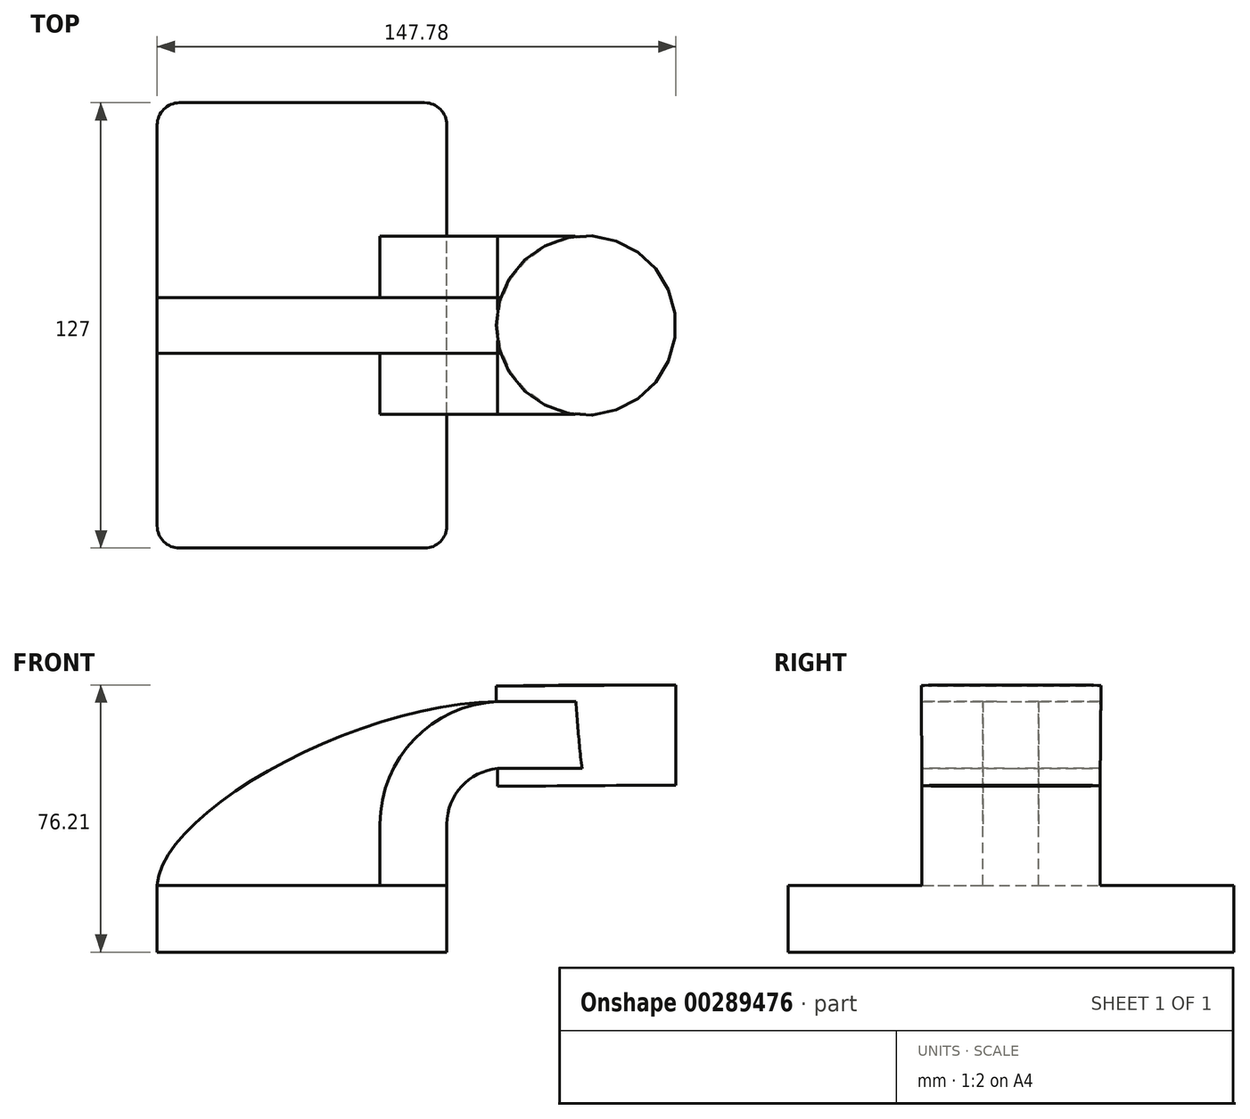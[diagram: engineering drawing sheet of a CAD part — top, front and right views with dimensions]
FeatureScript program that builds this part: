
annotation { "Feature Type Name" : "Feature", "Feature Type Description" : "" }
export const myFeature = defineFeature(function(context is Context, id is Id, definition is map)
    precondition{}
    {
        {
            var Q0;
            Q0=qCreatedBy(makeId("Front.planeOp"),FACE);
            var sketch = newSketch(context, id + "F0", { "sketchPlane" : qUnion([Q0])});
            skLineSegment(sketch, "E0.bottom", {"start": v(-41.28, 9.52) * mm, "end": v(41.27, 9.53) * mm});
            skLineSegment(sketch, "E0.top", {"start": v(-41.27, -9.53) * mm, "end": v(41.28, -9.53) * mm});
            skLineSegment(sketch, "E0.left", {"start": v(-41.28, 9.52) * mm, "end": v(-41.28, -9.53) * mm});
            skLineSegment(sketch, "E0.right", {"start": v(41.28, 9.53) * mm, "end": v(41.28, -9.52) * mm});
            skPoint(sketch, "E0.middle", {"position": v(0, 0) * mm});
            skLineSegment(sketch, "E1.bottom", {"start": v(55.7, 66.68) * mm, "end": v(106.5, 66.68) * mm});
            skLineSegment(sketch, "E1.top", {"start": v(55.7, 38.1) * mm, "end": v(106.5, 38.1) * mm});
            skLineSegment(sketch, "E1.left", {"start": v(55.7, 66.68) * mm, "end": v(55.7, 38.1) * mm});
            skLineSegment(sketch, "E1.right", {"start": v(106.5, 66.68) * mm, "end": v(106.5, 38.1) * mm});
            skPoint(sketch, "E1.middle", {"position": v(81.1, 52.39) * mm});
            skLineSegment(sketch, "E2", {"start": v(41.28, 9.53) * mm, "end": v(41.28, 27) * mm});
            skArc(sketch, "E3", {"start": v(41.28, 27) * mm, "mid": v(45.92, 38.23) * mm, "end": v(57.15, 42.88) * mm});
            skLineSegment(sketch, "E4", {"start": v(57.15, 42.88) * mm, "end": v(80.9, 42.88) * mm});
            skLineSegment(sketch, "E5.0", {"start": v(57.15, 61.93) * mm, "end": v(80.9, 61.93) * mm});
            skArc(sketch, "E5.1", {"start": v(22.23, 27) * mm, "mid": v(32.45, 51.7) * mm, "end": v(57.15, 61.93) * mm});
            skLineSegment(sketch, "E5.2", {"start": v(22.23, 9.53) * mm, "end": v(22.23, 27) * mm});
            skLineSegment(sketch, "E6", {"start": v(81.1, 38.1) * mm, "end": v(80.9, 66.68) * mm});
            skFitSpline(sketch, "E7", {"points": [v(-41.28, 9.52) * mm, v(57.15, 61.93) * mm], "startDerivative": vector(3.47, 63.91) * mm, "endDerivative": vector(119.87, -0.98) * mm});
            skSolve(sketch);
        }
        {
            var Q0;
            Q0=makeQuery(id+"F0.imprint","IMPRINT",FACE,{"disambiguationData":[TD([[makeQuery(id+"F0.imprint","IMPRINT",EDGE,{"derivedFrom":sQuery(id+"F0.wireOp",EDGE,"E0.top")}),1.0]])]});
            extrude(context, id + "F1", {"entities" : qUnion([Q0]), "endBound" : BoundingType.SYMMETRIC, "depth" : 127 * mm});
        }
        {
            var Q0;
            {var subQ1=sQuery(id+"F0.wireOp",EDGE,"E2");Q0=makeQuery(id+"F0.imprint","IMPRINT",FACE,{"disambiguationData":[TD([[makeQuery(id+"F0.imprint","IMPRINT",EDGE,{"derivedFrom":subQ1}),1.0]])]});}
            extrude(context, id + "F2", {"entities" : qUnion([Q0]), "operationType" : NewBodyOperationType.ADD, "endBound" : BoundingType.SYMMETRIC, "depth" : 50.8 * mm});
        }
        {
            var Q0;
            {var subQ0=sQuery(id+"F0.wireOp",EDGE,"E5.2");Q0=makeQuery(id+"F0.imprint","IMPRINT",FACE,{"disambiguationData":[TD([[makeQuery(id+"F0.imprint","IMPRINT",EDGE,{"derivedFrom":subQ0}),1.0]])]});}
            extrude(context, id + "F3", {"entities" : qUnion([Q0]), "operationType" : NewBodyOperationType.ADD, "endBound" : BoundingType.SYMMETRIC, "depth" : 15.88 * mm});
        }
        {
            var Q0;
            {var subQ0=sQuery(id+"F0.wireOp",EDGE,"E1.left");Q0=makeQuery(id+"F3.boolean.opBoolean","MERGE",FACE,{"derivedFrom":[makeQuery(id+"F2.opExtrude","SWEPT_FACE",FACE,{"disambiguationData":[OSD([subQ0])]}),makeQuery(id+"F3.opExtrude","SWEPT_FACE",FACE,{"disambiguationData":[OSD([subQ0])]})]});}
            extrude(context, id + "F4", {"entities" : qUnion([Q0]), "operationType" : NewBodyOperationType.ADD, "depth" : 25.4 * mm});
        }
        {
            var Q0;
            {var subQ0=sQuery(id+"F0.wireOp",EDGE,"E1.right");Q0=makeQuery(id+"F0.imprint","IMPRINT",FACE,{"disambiguationData":[TD([[makeQuery(id+"F0.imprint","IMPRINT",EDGE,{"derivedFrom":subQ0}),-1.0]])]});}
            var Q1;
            Q1=sQuery(id+"F0.wireOp",EDGE,"E6");
            revolve(context, id + "F5", {"operationType" : NewBodyOperationType.ADD, "entities" : qUnion([Q0]), "axis" : qUnion([Q1]), "revolveType" : RevolveType.FULL});
        }
        {
            var Q0;
            Q0=makeQuery(id+"F1.opExtrude","CAP_EDGE",EDGE,{"disambiguationData":[OSD([sQuery(id+"F0.wireOp",EDGE,"E0.left")])],"isStart":true});
            var Q1;
            Q1=makeQuery(id+"F1.opExtrude","CAP_EDGE",EDGE,{"disambiguationData":[OSD([sQuery(id+"F0.wireOp",EDGE,"E0.left")])],"isStart":false});
            var Q2;
            Q2=makeQuery(id+"F1.opExtrude","CAP_EDGE",EDGE,{"disambiguationData":[OSD([sQuery(id+"F0.wireOp",EDGE,"E0.right")])],"isStart":false});
            var Q3;
            Q3=makeQuery(id+"F1.opExtrude","CAP_EDGE",EDGE,{"disambiguationData":[OSD([sQuery(id+"F0.wireOp",EDGE,"E0.right")])],"isStart":true});
            fillet(context, id + "F6", {"entities" : qUnion([Q0, Q1, Q2, Q3]), "radius" : 6.35 * mm, "tangentPropagation" : true, "allowEdgeOverflow" : false});
        }
    });
